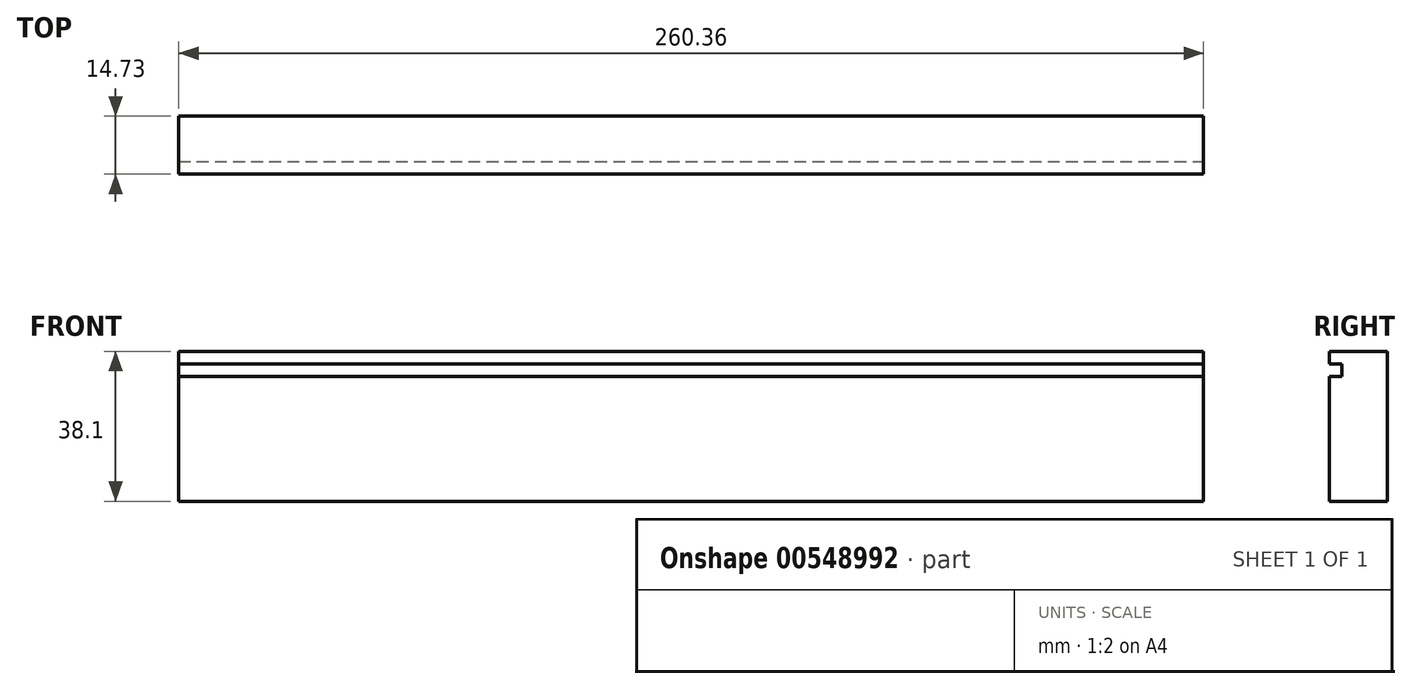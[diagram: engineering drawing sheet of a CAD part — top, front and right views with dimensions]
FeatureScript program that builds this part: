
annotation { "Feature Type Name" : "Feature", "Feature Type Description" : "" }
export const myFeature = defineFeature(function(context is Context, id is Id, definition is map)
    precondition{}
    {
        {
            var Q0;
            Q0=qCreatedBy(makeId("Front.planeOp"),FACE);
            var sketch = newSketch(context, id + "F0", { "sketchPlane" : qUnion([Q0])});
            skLineSegment(sketch, "E0.bottom", {"start": v(130.18, -19.05) * mm, "end": v(-130.18, -19.05) * mm});
            skLineSegment(sketch, "E0.top", {"start": v(130.18, 19.05) * mm, "end": v(-130.18, 19.05) * mm});
            skLineSegment(sketch, "E0.left", {"start": v(130.18, -19.05) * mm, "end": v(130.18, 19.05) * mm});
            skLineSegment(sketch, "E0.right", {"start": v(-130.18, -19.05) * mm, "end": v(-130.18, 19.05) * mm});
            skPoint(sketch, "E0.middle", {"position": v(0, 0) * mm});
            skSolve(sketch);
        }
        {
            var Q0;
            Q0 = qSketchRegion(id + "F0", true);
            extrude(context, id + "F1", {"entities" : qUnion([Q0]), "depth" : 14.73 * mm, "offsetDistance" : 25.4 * mm});
        }
        {
            var Q0;
            Q0=makeQuery(id+"F1.opExtrude","CAP_FACE",FACE,{"disambiguationData":[OSD([sQuery(id+"F0.wireOp",EDGE,"E0.bottom"),sQuery(id+"F0.wireOp",EDGE,"E0.top"),sQuery(id+"F0.wireOp",EDGE,"E0.left"),sQuery(id+"F0.wireOp",EDGE,"E0.right")])],"isStart":false});
            var sketch = newSketch(context, id + "F2", { "sketchPlane" : qUnion([Q0])});
            skLineSegment(sketch, "E1.bottom", {"start": v(-130.18, 15.88) * mm, "end": v(130.18, 15.88) * mm});
            skLineSegment(sketch, "E1.top", {"start": v(-130.18, 12.7) * mm, "end": v(130.18, 12.7) * mm});
            skLineSegment(sketch, "E1.left", {"start": v(-130.18, 15.88) * mm, "end": v(-130.18, 12.7) * mm});
            skLineSegment(sketch, "E1.right", {"start": v(130.18, 15.88) * mm, "end": v(130.18, 12.7) * mm});
            skSolve(sketch);
        }
        {
            var Q0;
            Q0 = qSketchRegion(id + "F2", true);
            extrude(context, id + "F3", {"entities" : qUnion([Q0]), "operationType" : NewBodyOperationType.REMOVE, "oppositeDirection" : true, "depth" : 3.17 * mm, "offsetDistance" : 25.4 * mm});
        }
    });
